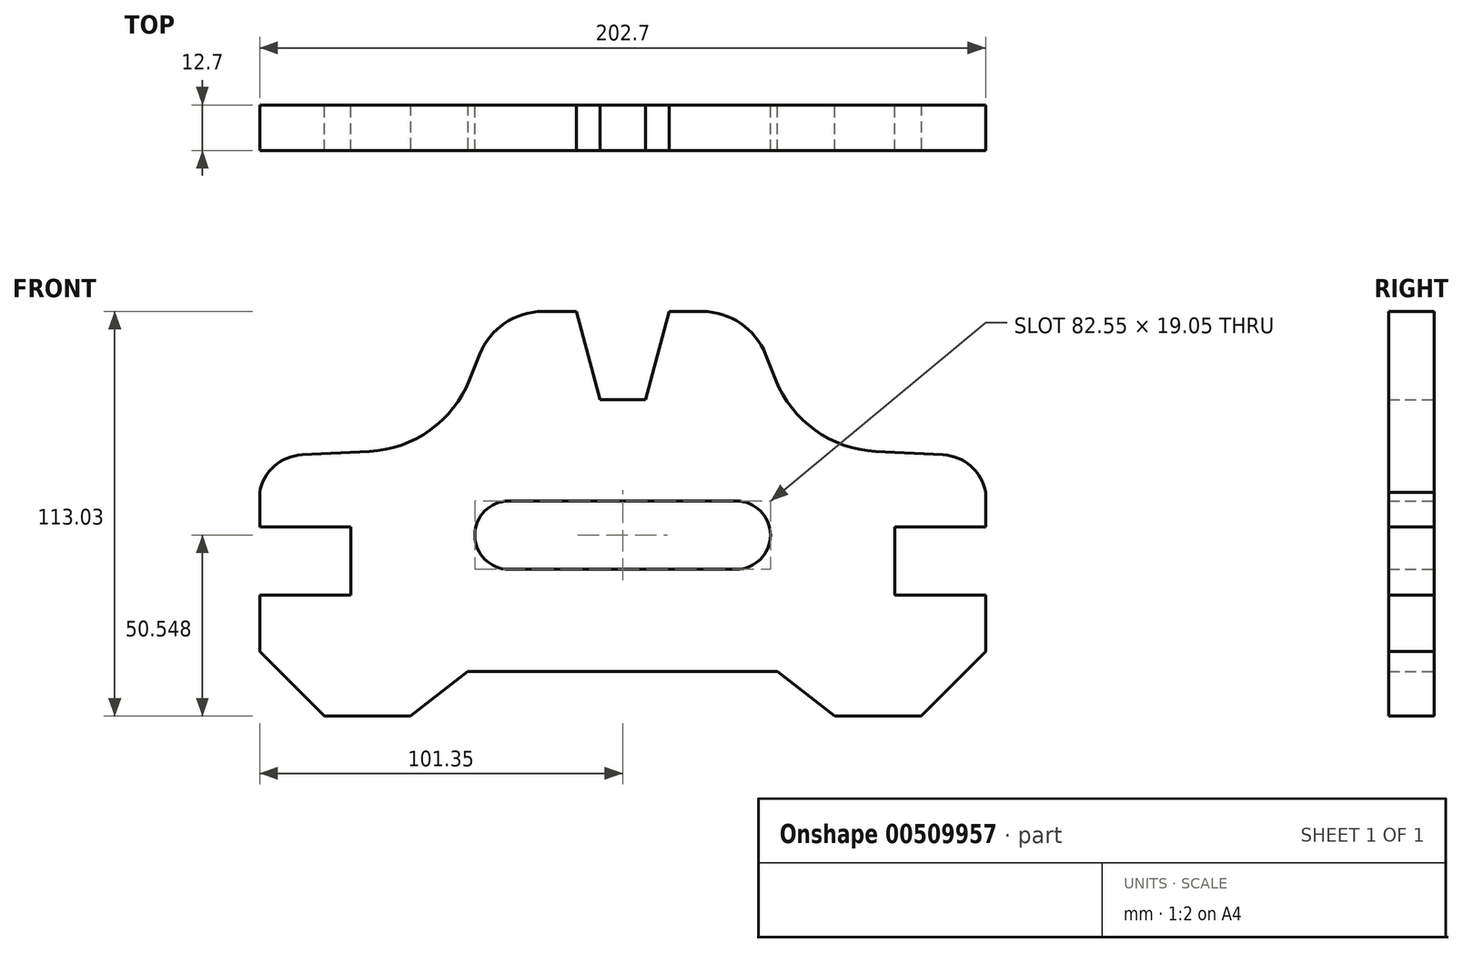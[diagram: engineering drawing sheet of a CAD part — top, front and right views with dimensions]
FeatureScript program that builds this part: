
annotation { "Feature Type Name" : "Feature", "Feature Type Description" : "" }
export const myFeature = defineFeature(function(context is Context, id is Id, definition is map)
    precondition{}
    {
        {
            var Q0;
            Q0=qCreatedBy(makeId("Front.planeOp"),FACE);
            var sketch = newSketch(context, id + "F0", { "sketchPlane" : qUnion([Q0])});
            skLineSegment(sketch, "E0", {"start": v(0, 80.89) * mm, "end": v(0, -67.47) * mm, "construction": true});
            skLineSegment(sketch, "E1", {"start": v(-6.37, 54.24) * mm, "end": v(6.35, 54.24) * mm});
            skLineSegment(sketch, "E2", {"start": v(6.35, 54.24) * mm, "end": v(12.95, 78.88) * mm});
            skLineSegment(sketch, "E3", {"start": v(12.95, 78.88) * mm, "end": v(22.25, 78.88) * mm});
            skArc(sketch, "E4", {"start": v(22.25, 78.88) * mm, "mid": v(32.96, 75.6) * mm, "end": v(39.96, 66.85) * mm});
            skLineSegment(sketch, "E5", {"start": v(39.96, 66.85) * mm, "end": v(42.75, 59.83) * mm});
            skArc(sketch, "E6", {"start": v(42.75, 59.83) * mm, "mid": v(53.76, 45.73) * mm, "end": v(70.64, 39.83) * mm});
            skLineSegment(sketch, "E7", {"start": v(70.64, 39.83) * mm, "end": v(89.48, 38.86) * mm});
            skArc(sketch, "E8", {"start": v(89.48, 38.86) * mm, "mid": v(97.26, 35.68) * mm, "end": v(101.35, 28.34) * mm});
            skLineSegment(sketch, "E9", {"start": v(101.35, 28.34) * mm, "end": v(101.35, 18.68) * mm});
            skLineSegment(sketch, "E10", {"start": v(101.35, 18.68) * mm, "end": v(75.95, 18.68) * mm});
            skLineSegment(sketch, "E11", {"start": v(75.95, 18.68) * mm, "end": v(75.95, -0.37) * mm});
            skLineSegment(sketch, "E12", {"start": v(75.95, -0.37) * mm, "end": v(101.35, -0.37) * mm});
            skLineSegment(sketch, "E13", {"start": v(101.35, -0.37) * mm, "end": v(101.35, -34.15) * mm});
            skLineSegment(sketch, "E14", {"start": v(101.35, -34.15) * mm, "end": v(45.21, -34.15) * mm});
            skLineSegment(sketch, "E15", {"start": v(45.21, -34.15) * mm, "end": v(42.03, -21.7) * mm});
            skLineSegment(sketch, "E16.MirrorCS", {"start": v(-6.35, 54.24) * mm, "end": v(-12.95, 78.88) * mm});
            skLineSegment(sketch, "E17.MirrorCS", {"start": v(-12.95, 78.88) * mm, "end": v(-22.25, 78.88) * mm});
            skArc(sketch, "E18.MirrorCS", {"start": v(-22.25, 78.88) * mm, "mid": v(-32.96, 75.6) * mm, "end": v(-39.96, 66.85) * mm});
            skLineSegment(sketch, "E19.MirrorCS", {"start": v(-39.96, 66.85) * mm, "end": v(-42.75, 59.83) * mm});
            skArc(sketch, "E20.MirrorCS", {"start": v(-42.75, 59.83) * mm, "mid": v(-53.76, 45.73) * mm, "end": v(-70.64, 39.83) * mm});
            skLineSegment(sketch, "E21.MirrorCS", {"start": v(-70.64, 39.83) * mm, "end": v(-89.48, 38.86) * mm});
            skArc(sketch, "E22.MirrorCS", {"start": v(-89.48, 38.86) * mm, "mid": v(-97.26, 35.68) * mm, "end": v(-101.35, 28.34) * mm});
            skLineSegment(sketch, "E23.MirrorCS", {"start": v(-101.35, 28.34) * mm, "end": v(-101.35, 18.68) * mm});
            skLineSegment(sketch, "E24.MirrorCS", {"start": v(-101.35, 18.68) * mm, "end": v(-75.95, 18.68) * mm});
            skLineSegment(sketch, "E25.MirrorCS", {"start": v(-75.95, 18.68) * mm, "end": v(-75.95, -0.37) * mm});
            skLineSegment(sketch, "E26.MirrorCS", {"start": v(-75.95, -0.37) * mm, "end": v(-101.35, -0.37) * mm});
            skLineSegment(sketch, "E27.MirrorCS", {"start": v(-101.35, -0.37) * mm, "end": v(-101.35, -34.15) * mm});
            skLineSegment(sketch, "E28.MirrorCS", {"start": v(-101.35, -34.15) * mm, "end": v(-45.21, -34.15) * mm});
            skLineSegment(sketch, "E29.MirrorCS", {"start": v(-45.21, -34.15) * mm, "end": v(-42.03, -21.7) * mm});
            skLineSegment(sketch, "E30", {"start": v(42.03, -21.7) * mm, "end": v(0, -21.7) * mm});
            skLineSegment(sketch, "E31", {"start": v(0, -21.7) * mm, "end": v(-42.03, -21.7) * mm});
            skLineSegment(sketch, "E32", {"start": v(-31.75, 25.92) * mm, "end": v(31.75, 25.92) * mm});
            skLineSegment(sketch, "E33", {"start": v(-31.75, 6.87) * mm, "end": v(31.75, 6.87) * mm});
            skArc(sketch, "E34", {"start": v(31.75, 25.92) * mm, "mid": v(41.28, 16.4) * mm, "end": v(31.75, 6.87) * mm});
            skArc(sketch, "E35", {"start": v(-31.75, 25.92) * mm, "mid": v(-41.28, 16.4) * mm, "end": v(-31.75, 6.87) * mm});
            skSolve(sketch);
        }
        {
            var Q0;
            Q0 = qSketchRegion(id + "F0", true);
            extrude(context, id + "F1", {"entities" : qUnion([Q0]), "depth" : 12.7 * mm, "offsetDistance" : 25.4 * mm});
        }
        {
            var Q0;
            Q0=makeQuery(id+"F1.opExtrude","SWEPT_EDGE",EDGE,{"disambiguationData":[OSD([sQuery(id+"F0.wireOp",EDGE,"E27.MirrorCS"),sQuery(id+"F0.wireOp",EDGE,"E28.MirrorCS")])]});
            var Q1;
            Q1=makeQuery(id+"F1.opExtrude","SWEPT_EDGE",EDGE,{"disambiguationData":[OSD([sQuery(id+"F0.wireOp",EDGE,"E13"),sQuery(id+"F0.wireOp",EDGE,"E14")])]});
            var Q2;
            Q2=makeQuery(id+"F1.opExtrude","SWEPT_EDGE",EDGE,{"disambiguationData":[OSD([sQuery(id+"F0.wireOp",EDGE,"E28.MirrorCS"),sQuery(id+"F0.wireOp",EDGE,"E29.MirrorCS")])]});
            var Q3;
            Q3=makeQuery(id+"F1.opExtrude","SWEPT_EDGE",EDGE,{"disambiguationData":[OSD([sQuery(id+"F0.wireOp",EDGE,"E14"),sQuery(id+"F0.wireOp",EDGE,"E15")])]});
            chamfer(context, id + "F2", {"entities" : qUnion([Q0, Q1, Q2, Q3]), "width" : 18.03 * mm, "tangentPropagation" : true});
        }
    });
